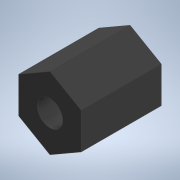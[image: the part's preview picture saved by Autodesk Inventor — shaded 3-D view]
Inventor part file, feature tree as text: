
AUTODESK INVENTOR PART (.ipt)
format: ipt  version: 2020 (Build 240168000, 168)  size: 96,768 bytes
history: native  units: mm
features: extrude x1, sketch x1
ambient origin geometry x8: Origin, YZ Plane, XZ Plane, XY Plane, X Axis, Y Axis, Z Axis, Center Point
bodies: Solid1 (feature_tree)
feature tree (2):
  extrude  "Extrusion1"  Depth=4.5mm
  sketch  "Sketch1"  dims[d0=3.2mm d1=4.5mm d2=10.0mm d3=0.0mm]
